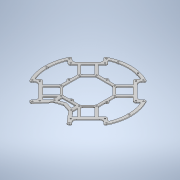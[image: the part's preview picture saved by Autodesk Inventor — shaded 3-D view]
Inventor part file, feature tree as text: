
AUTODESK INVENTOR PART (.ipt)
format: ipt  version: 2020 (Build 240168000, 168)  size: 1,227,776 bytes
history: native  units: mm
features: extrude x10, sketch x7, projected_geometry x6, other x1
ambient origin geometry x8: Origin, YZ Plane, XZ Plane, XY Plane, X Axis, Y Axis, Z Axis, Center Point
bodies: Body1 (feature_tree)
feature tree (24):
  other  "Твердое тело1"
  extrude  "outer"  TaperAngle=45.0deg  [1 undecoded]
  extrude  "inner"  Depth=7.0mm
  sketch  "Эскиз3"
  extrude  "Выдавливание3"  Depth=20.0mm
  extrude  "Выдавливание4"  Depth=7.0mm
  sketch  "Эскиз4"
  extrude  "Выдавливание5"  Depth=3.2mm
  extrude  "Выдавливание6"  Depth=59.0mm
  sketch  "Эскиз5"
  extrude  "Выдавливание7"  Depth=83.0mm
  extrude  "Выдавливание8"  Depth=69.0mm
  extrude  "Выдавливание9"  Depth=55.0mm
  extrude  "Выдавливание10"  Depth=3.0mm
  sketch  "Эскиз1"
  sketch  "Эскиз2"
  projected_geometry  "Спроецированная петля1"
  projected_geometry  "Спроецированная петля2"
  projected_geometry  "Спроецированная петля3"
  projected_geometry  "Спроецированная петля4"
  sketch  "Эскиз6"
  projected_geometry  "Спроецированная петля5"
  sketch  "Эскиз7"
  projected_geometry  "Спроецированная петля6"
note: 1 required parameter value undecoded (feature->parameter linkage not recoverable at this tier; creation-order binding heuristic only, values carry confidence <= 0.55)
